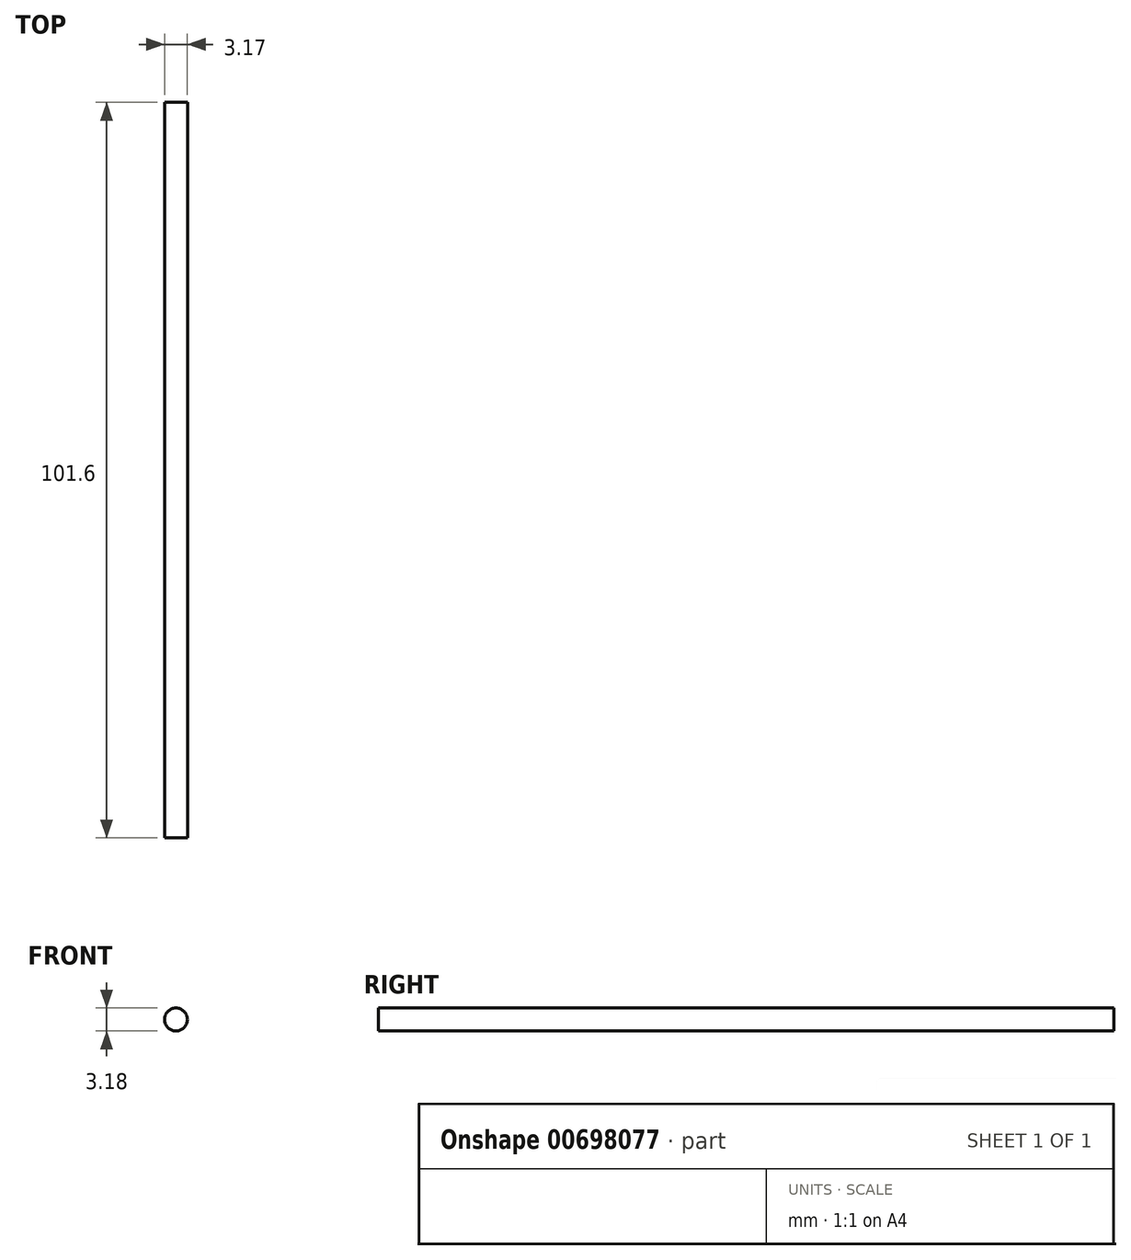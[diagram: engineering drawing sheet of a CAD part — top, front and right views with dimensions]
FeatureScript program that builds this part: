
annotation { "Feature Type Name" : "Feature", "Feature Type Description" : "" }
export const myFeature = defineFeature(function(context is Context, id is Id, definition is map)
    precondition{}
    {
        {
            var Q0;
            Q0=qCreatedBy(makeId("Front.planeOp"),FACE);
            var sketch = newSketch(context, id + "F0", { "sketchPlane" : qUnion([Q0])});
            skCircle(sketch, "E0", {"center": v(-22.6, 5.97) * mm, "radius": 1.59 * mm});
            skSolve(sketch);
        }
        {
            var Q0;
            Q0=makeQuery(id+"F0.imprint","IMPRINT",FACE,{"disambiguationData":[TD([[makeQuery(id+"F0.imprint","IMPRINT",EDGE,{"derivedFrom":sQuery(id+"F0.wireOp",EDGE,"E0")}),1.0]])]});
            extrude(context, id + "F1", {"entities" : qUnion([Q0]), "depth" : 101.6 * mm, "offsetDistance" : 25.4 * mm});
        }
    });
